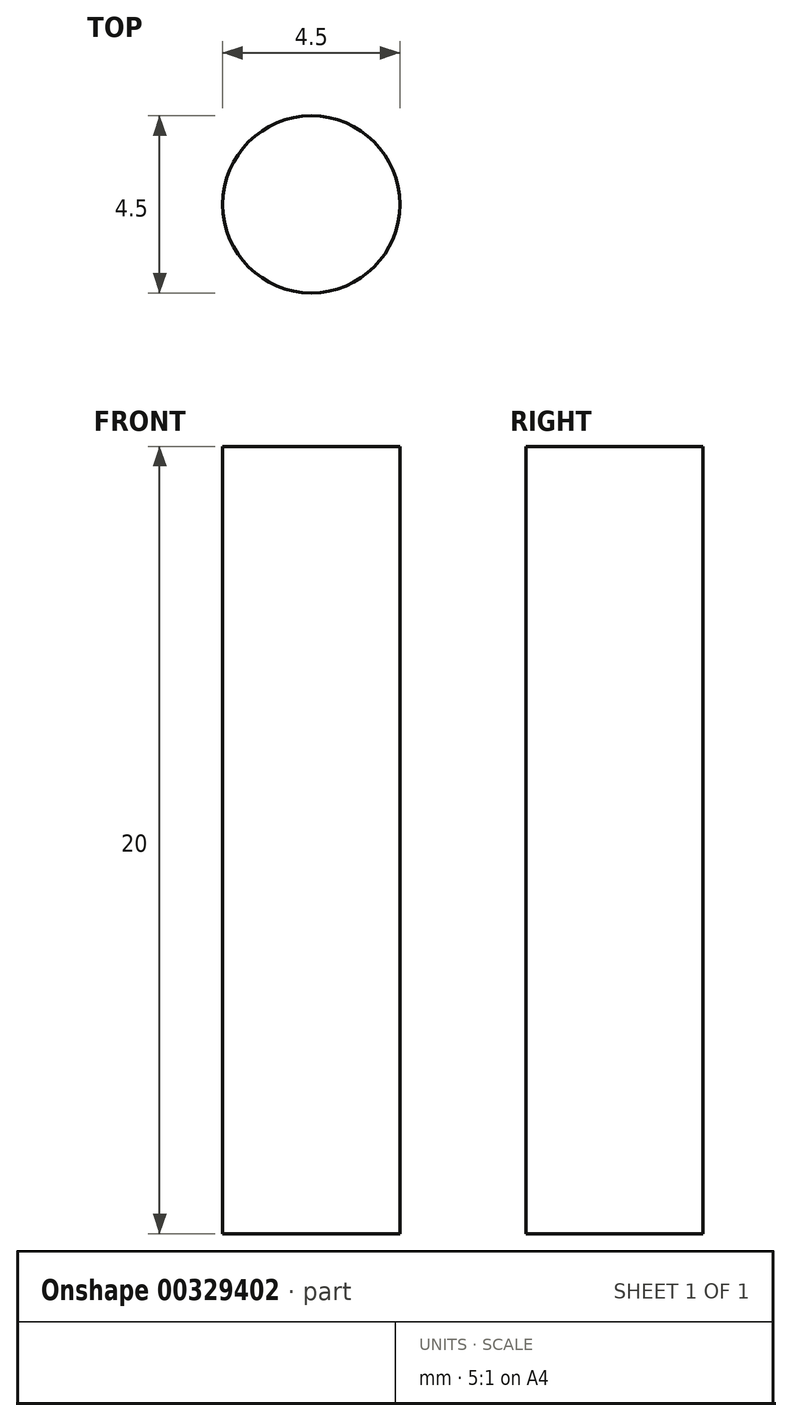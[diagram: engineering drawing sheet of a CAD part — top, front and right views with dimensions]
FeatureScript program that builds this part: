
annotation { "Feature Type Name" : "Feature", "Feature Type Description" : "" }
export const myFeature = defineFeature(function(context is Context, id is Id, definition is map)
    precondition{}
    {
        {
            var Q0;
            Q0=qCreatedBy(makeId("Top.planeOp"),FACE);
            var sketch = newSketch(context, id + "F0", { "sketchPlane" : qUnion([Q0])});
            skCircle(sketch, "E0", {"center": v(0, 0) * mm, "radius": 2.25 * mm});
            skSolve(sketch);
        }
        {
            var Q0;
            Q0=makeQuery(id+"F0.imprint","IMPRINT",FACE,{"disambiguationData":[TD([[makeQuery(id+"F0.imprint","IMPRINT",EDGE,{"derivedFrom":sQuery(id+"F0.wireOp",EDGE,"E0")}),1.0]])]});
            extrude(context, id + "F1", {"entities" : qUnion([Q0]), "depth" : 20 * mm});
        }
    });
